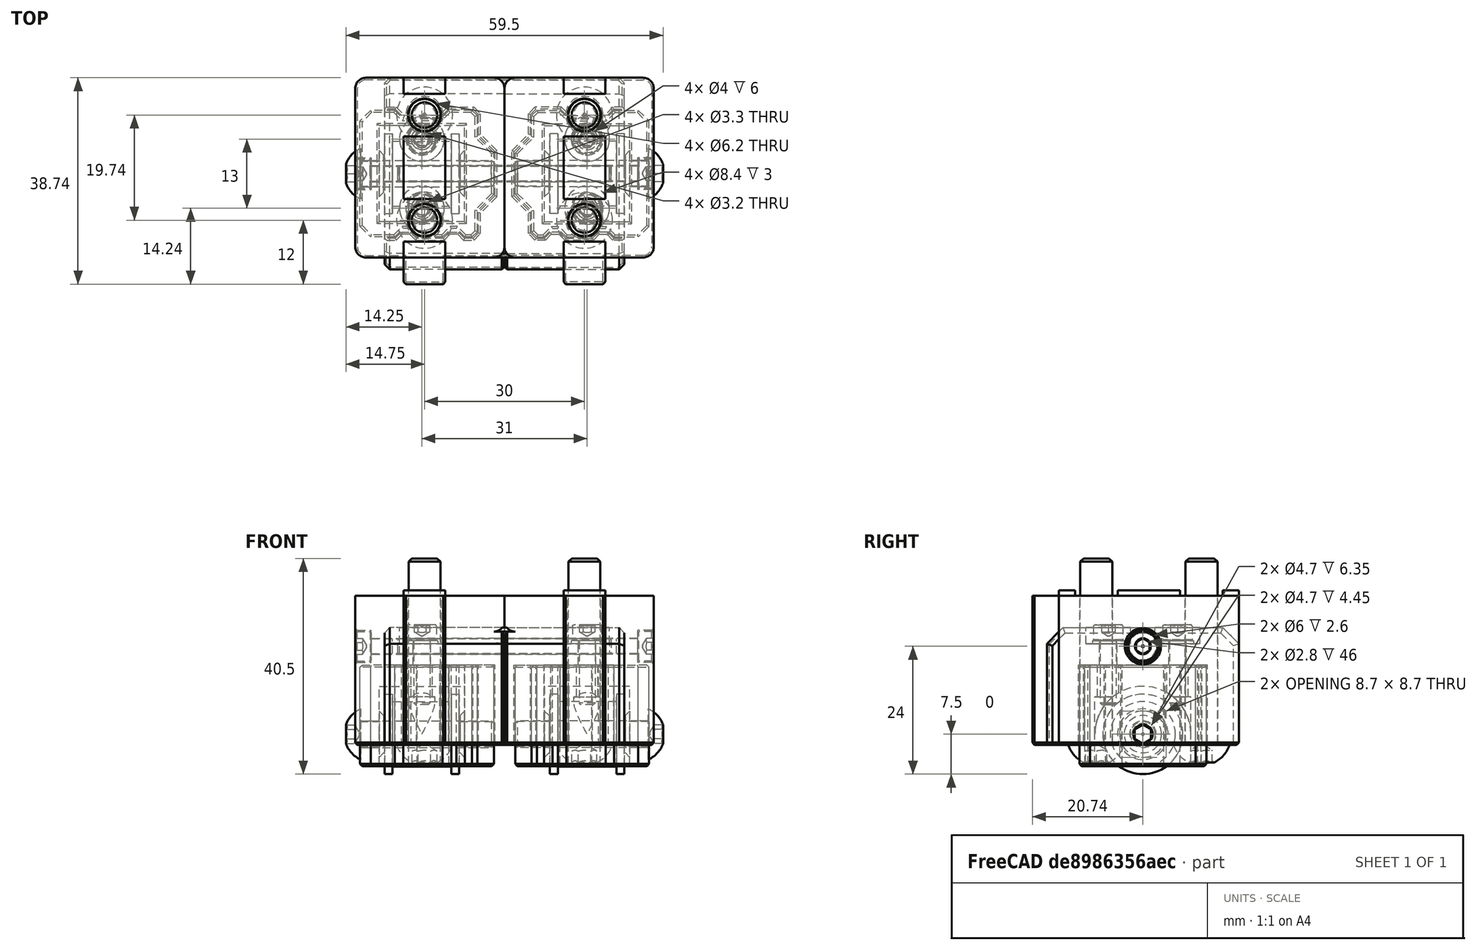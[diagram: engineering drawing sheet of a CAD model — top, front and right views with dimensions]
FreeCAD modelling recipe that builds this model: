
FCSTD DOCUMENT  (FreeCAD 0.19R24291 (Git))
Label: z-idler-assembly
License: Other
LicenseURL: GPL3
objects: Part::FeaturePython×16, Part::Feature×6, App::Part×2
note: 22 computed .brp shape members not serialized (recipe doc carries the construction recipe); baked Part::Feature solids carry a one-line shape summary decoded from their .brp

FEATURE [Part::Feature] Fusion013005011003002  label="20t-9mm-pulley002"
  Placement = pos=(0,0,-1) rot=(0,0,1;0rad)
  shape: bbox 14 x 15 x 15 mm, 7 faces (baked)
FEATURE [Part::Feature] Part__Mirroring002002  label="20t-9mm-pulley003"
  Placement = pos=(0,0,-1) rot=(0,0,1;0rad)
  shape: bbox 14 x 15 x 15 mm, 7 faces (baked)
FEATURE [Part::FeaturePython] Screw  label="M3x45-Screw"  # Fasteners workbench fastener (typed FeaturePython)
  Placement = pos=(-25,0,18.5) rot=(0,-1,0;1.5708rad)
  diameter = 4
  invert = true
  length = 10
  lengthCustom = 45
  matchOuter = true
  offset = 0
  thread = false
  type = 33
FEATURE [Part::FeaturePython] Screw001  label="M6x35-Screw"  # Fasteners workbench fastener (typed FeaturePython)
  Placement = pos=(-15,11,0) rot=(1,0,0;3.14159rad)
  diameter = 4
  invert = true
  length = 13
  lengthCustom = 35
  matchOuter = true
  offset = 0
  thread = false
  type = 39
FEATURE [Part::FeaturePython] Screw002  label="M6x35-Screw001"  # Fasteners workbench fastener (typed FeaturePython)
  Placement = pos=(-15,-8.74,0) rot=(1,0,0;3.14159rad)
  diameter = 4
  invert = true
  length = 13
  lengthCustom = 35
  matchOuter = true
  offset = 0
  thread = false
  type = 39
FEATURE [Part::FeaturePython] Washer001  label="M3-Washer006"  # Fasteners workbench fastener (typed FeaturePython)
  Placement = pos=(15.5,-6.5,19) rot=(0,0,1;0rad)
  diameter = 4
  invert = false
  matchOuter = true
  offset = 0
  type = 5
FEATURE [Part::FeaturePython] Washer  label="M3-Washer"  # Fasteners workbench fastener (typed FeaturePython)
  Placement = pos=(15.5,6.5,19) rot=(0,0,1;0rad)
  diameter = 4
  invert = false
  matchOuter = true
  offset = 0
  type = 5
FEATURE [Part::FeaturePython] Screw003  label="M3x12-Screw004"  # Fasteners workbench fastener (typed FeaturePython)
  Placement = pos=(15.5,6.5,19.55) rot=(0,0,1;0rad)
  baseObject = -> Washer [Edge1]
  diameter = 4
  invert = false
  length = 10
  lengthCustom = 12
  matchOuter = true
  offset = 0
  thread = false
  type = 33
FEATURE [Part::FeaturePython] Screw004  label="M3x12-Screw005"  # Fasteners workbench fastener (typed FeaturePython)
  Placement = pos=(15.5,-6.5,19.55) rot=(0,0,1;0rad)
  baseObject = -> Washer001 [Edge1]
  diameter = 4
  invert = false
  length = 10
  lengthCustom = 12
  matchOuter = true
  offset = 0
  thread = false
  type = 33
FEATURE [Part::FeaturePython] Washer002  label="M3-Washer007"  # Fasteners workbench fastener (typed FeaturePython)
  Placement = pos=(-15.5,6.5,19) rot=(0,0,1;0rad)
  diameter = 4
  invert = true
  matchOuter = true
  offset = 0
  type = 5
FEATURE [Part::FeaturePython] Washer003  label="M3-Washer008"  # Fasteners workbench fastener (typed FeaturePython)
  Placement = pos=(-15.5,-6.5,19) rot=(0,0,1;0rad)
  diameter = 4
  invert = true
  matchOuter = true
  offset = 0
  type = 5
FEATURE [Part::FeaturePython] Screw005  label="M3x45-Screw001"  # Fasteners workbench fastener (typed FeaturePython)
  Placement = pos=(25,0,18.5) rot=(0,1,0;1.5708rad)
  diameter = 4
  invert = false
  length = 10
  lengthCustom = 45
  matchOuter = true
  offset = 0
  thread = false
  type = 33
FEATURE [Part::FeaturePython] Screw006  label="M6x35-Screw003"  # Fasteners workbench fastener (typed FeaturePython)
  Placement = pos=(15,-8.74,0) rot=(1,0,0;3.14159rad)
  diameter = 4
  invert = false
  length = 13
  lengthCustom = 35
  matchOuter = true
  offset = 0
  thread = false
  type = 39
FEATURE [Part::FeaturePython] Screw007  label="M6x35-Screw002"  # Fasteners workbench fastener (typed FeaturePython)
  Placement = pos=(15,11,0) rot=(1,0,0;3.14159rad)
  diameter = 4
  invert = false
  length = 13
  lengthCustom = 35
  matchOuter = true
  offset = 0
  thread = false
  type = 39
FEATURE [Part::FeaturePython] Screw008  label="M3x12-Screw"  # Fasteners workbench fastener (typed FeaturePython)
  Placement = pos=(-15.5,6.5,19.55) rot=(0,0,1;0rad)
  baseObject = -> Washer002 [Edge1]
  diameter = 4
  invert = false
  length = 10
  lengthCustom = 12
  matchOuter = true
  offset = 0
  thread = false
  type = 33
FEATURE [Part::FeaturePython] Screw009  label="M3x12-Screw006"  # Fasteners workbench fastener (typed FeaturePython)
  Placement = pos=(-15.5,-6.5,19.55) rot=(0,0,1;0rad)
  baseObject = -> Washer003 [Edge1]
  diameter = 4
  invert = false
  length = 10
  lengthCustom = 12
  matchOuter = true
  offset = 0
  thread = false
  type = 33
FEATURE [Part::FeaturePython] Screw010  label="M5x25-Screw001"  # Fasteners workbench fastener (typed FeaturePython)
  Placement = pos=(-27,0,2) rot=(0,-1,0;1.5708rad)
  diameter = 3
  invert = false
  length = 6
  lengthCustom = 25
  matchOuter = true
  offset = 0
  thread = false
  type = 39
FEATURE [Part::FeaturePython] Screw011  label="M5x25-Screw"  # Fasteners workbench fastener (typed FeaturePython)
  Placement = pos=(27,0,2) rot=(0,1,0;1.5708rad)
  diameter = 3
  invert = true
  length = 6
  lengthCustom = 25
  matchOuter = true
  offset = 0
  thread = false
  type = 39
FEATURE [Part::Feature] Chamfer003068012003
  Placement = pos=(0,0,-4) rot=(0,0,1;0rad)
  shape: bbox 25.1 x 23.8 x 19 mm, 95 faces (baked)
FEATURE [Part::Feature] Part__Mirroring002006001  label="Chamfer003068012001 (Mirror #2)001"
  shape: bbox 25.1 x 23.8 x 19 mm, 95 faces (baked)
FEATURE [Part::Feature] Chamfer003068012002002
  shape: bbox 50.5 x 38.74 x 29 mm, 120 faces (baked)
FEATURE [App::Part] Part  label="Z-idler-left"
  Group = -> [Fusion013005011003002,Washer001,Screw001,Screw002,Screw003,Washer,Screw004,Screw,Screw011,Chamfer003068012003,Chamfer003068012002002]
  Origin = -> Origin
FEATURE [Part::Feature] Part__Mirroring002006002  label="Chamfer003068012002001 (Mirror #1)001"
  Placement = pos=(0,0,0) rot=(0,0,1;3.14159rad)
  shape: bbox 50.5 x 38.74 x 29 mm, 120 faces (baked)
FEATURE [App::Part] Part001  label="Z-idler-right"
  Group = -> [Part__Mirroring002002,Screw005,Screw007,Screw006,Screw008,Screw009,Washer003,Washer002,Screw010,Part__Mirroring002006001,Part__Mirroring002006002]
  Origin = -> Origin001
